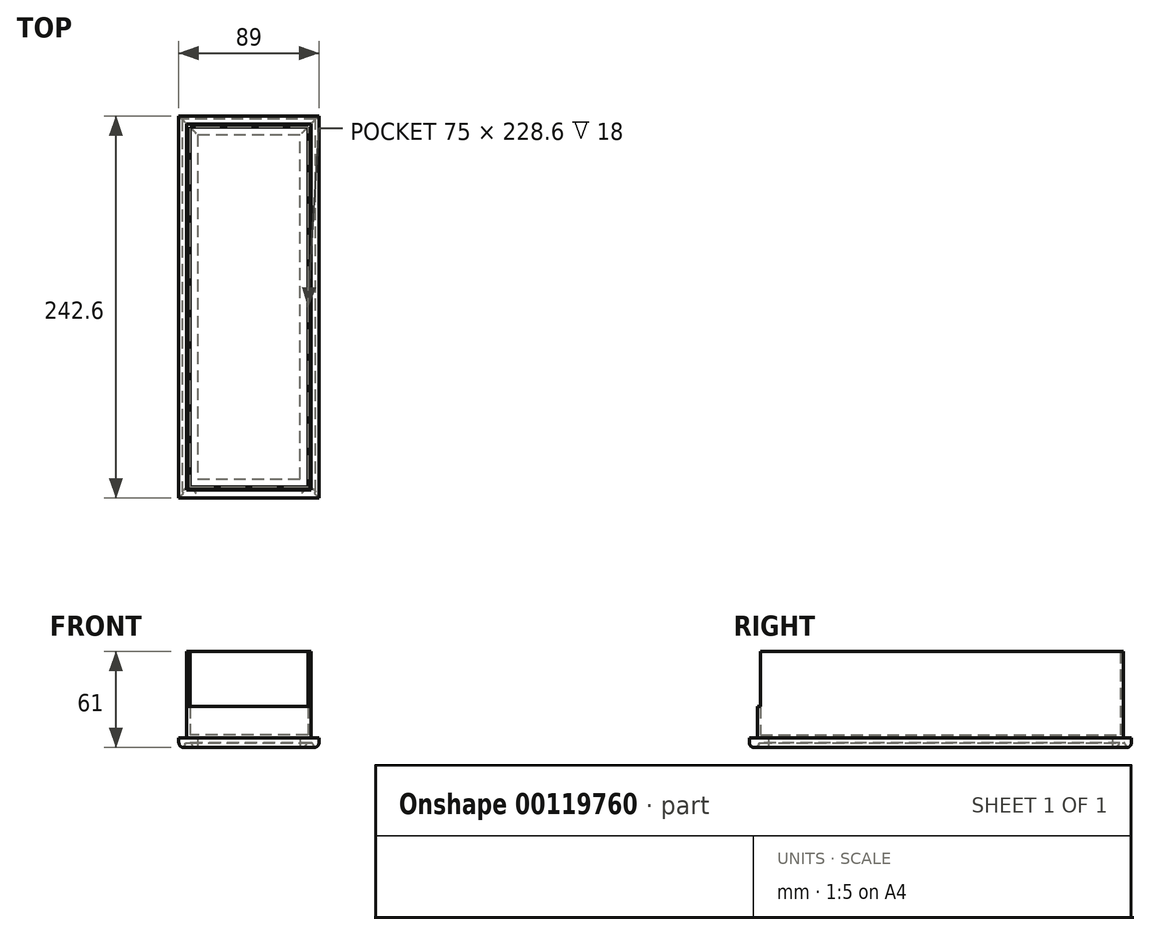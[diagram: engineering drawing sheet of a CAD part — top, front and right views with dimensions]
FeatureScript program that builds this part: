
annotation { "Feature Type Name" : "Feature", "Feature Type Description" : "" }
export const myFeature = defineFeature(function(context is Context, id is Id, definition is map)
    precondition{}
    {
        {
            var Q0;
            Q0=qCreatedBy(makeId("Top.planeOp"),FACE);
            var sketch = newSketch(context, id + "F0", { "sketchPlane" : qUnion([Q0])});
            skLineSegment(sketch, "E0.bottom", {"start": v(37.5, -114.3) * mm, "end": v(-37.5, -114.3) * mm});
            skLineSegment(sketch, "E0.top", {"start": v(37.5, 114.3) * mm, "end": v(-37.5, 114.3) * mm});
            skLineSegment(sketch, "E0.left", {"start": v(37.5, -114.3) * mm, "end": v(37.5, 114.3) * mm});
            skLineSegment(sketch, "E0.right", {"start": v(-37.5, -114.3) * mm, "end": v(-37.5, 114.3) * mm});
            skPoint(sketch, "E0.middle", {"position": v(0, 0) * mm});
            skSolve(sketch);
        }
        {
            var Q0;
            Q0 = qSketchRegion(id + "F0", true);
            extrude(context, id + "F1", {"entities" : qUnion([Q0]), "depth" : 2 * mm});
        }
        {
            var Q0;
            Q0=makeQuery(id+"F1.opExtrude","SWEPT_FACE",FACE,{"disambiguationData":[OSD([sQuery(id+"F0.wireOp",EDGE,"E0.right")])]});
            var sketch = newSketch(context, id + "F2", { "sketchPlane" : qUnion([Q0])});
            skLineSegment(sketch, "E1.bottom", {"start": v(-114.3, 0) * mm, "end": v(114.3, 0) * mm});
            skLineSegment(sketch, "E1.top", {"start": v(-114.3, 55) * mm, "end": v(114.3, 55) * mm});
            skLineSegment(sketch, "E1.left", {"start": v(-114.3, 0) * mm, "end": v(-114.3, 55) * mm});
            skLineSegment(sketch, "E1.right", {"start": v(114.3, 0) * mm, "end": v(114.3, 55) * mm});
            skSolve(sketch);
        }
        {
            var Q0;
            Q0 = qSketchRegion(id + "F2", true);
            extrude(context, id + "F3", {"entities" : qUnion([Q0]), "operationType" : NewBodyOperationType.ADD, "depth" : 2 * mm});
        }
        {
            var Q0;
            Q0=makeQuery(id+"F3.boolean.opBoolean","MERGE",FACE,{"derivedFrom":[makeQuery(id+"F1.opExtrude","SWEPT_FACE",FACE,{"disambiguationData":[OSD([sQuery(id+"F0.wireOp",EDGE,"E0.top")])]}),makeQuery(id+"F3.opExtrude","SWEPT_FACE",FACE,{"disambiguationData":[OSD([sQuery(id+"F2.wireOp",EDGE,"E1.left")])]})]});
            var sketch = newSketch(context, id + "F4", { "sketchPlane" : qUnion([Q0])});
            skLineSegment(sketch, "E2.bottom", {"start": v(39.5, 0) * mm, "end": v(-37.5, 0) * mm});
            skLineSegment(sketch, "E2.top", {"start": v(39.5, 55) * mm, "end": v(-37.5, 55) * mm});
            skLineSegment(sketch, "E2.left", {"start": v(39.5, 0) * mm, "end": v(39.5, 55) * mm});
            skLineSegment(sketch, "E2.right", {"start": v(-37.5, 0) * mm, "end": v(-37.5, 55) * mm});
            skSolve(sketch);
        }
        {
            var Q0;
            Q0 = qSketchRegion(id + "F4", true);
            extrude(context, id + "F5", {"entities" : qUnion([Q0]), "operationType" : NewBodyOperationType.ADD, "depth" : 2 * mm});
        }
        {
            var Q0;
            Q0=makeQuery(id+"F5.boolean.opBoolean","MERGE",FACE,{"derivedFrom":[makeQuery(id+"F1.opExtrude","SWEPT_FACE",FACE,{"disambiguationData":[OSD([sQuery(id+"F0.wireOp",EDGE,"E0.left")])]}),makeQuery(id+"F5.opExtrude","SWEPT_FACE",FACE,{"disambiguationData":[OSD([sQuery(id+"F4.wireOp",EDGE,"E2.right")])]})]});
            var sketch = newSketch(context, id + "F6", { "sketchPlane" : qUnion([Q0])});
            skLineSegment(sketch, "E3.bottom", {"start": v(116.3, 0) * mm, "end": v(-114.3, 0) * mm});
            skLineSegment(sketch, "E3.top", {"start": v(116.3, 55) * mm, "end": v(-114.3, 55) * mm});
            skLineSegment(sketch, "E3.left", {"start": v(116.3, 0) * mm, "end": v(116.3, 55) * mm});
            skLineSegment(sketch, "E3.right", {"start": v(-114.3, 0) * mm, "end": v(-114.3, 55) * mm});
            skSolve(sketch);
        }
        {
            var Q0;
            Q0 = qSketchRegion(id + "F6", true);
            extrude(context, id + "F7", {"entities" : qUnion([Q0]), "operationType" : NewBodyOperationType.ADD, "depth" : 2 * mm});
        }
        {
            var Q0;
            Q0=makeQuery(id+"F7.boolean.opBoolean","MERGE",FACE,{"derivedFrom":[makeQuery(id+"F3.boolean.opBoolean","MERGE",FACE,{"derivedFrom":[makeQuery(id+"F1.opExtrude","SWEPT_FACE",FACE,{"disambiguationData":[OSD([sQuery(id+"F0.wireOp",EDGE,"E0.bottom")])]}),makeQuery(id+"F3.opExtrude","SWEPT_FACE",FACE,{"disambiguationData":[OSD([sQuery(id+"F2.wireOp",EDGE,"E1.right")])]})]}),makeQuery(id+"F7.opExtrude","SWEPT_FACE",FACE,{"disambiguationData":[OSD([sQuery(id+"F6.wireOp",EDGE,"E3.right")])]})]});
            var sketch = newSketch(context, id + "F8", { "sketchPlane" : qUnion([Q0])});
            skLineSegment(sketch, "E4.bottom", {"start": v(-39.5, 0) * mm, "end": v(39.5, 0) * mm});
            skLineSegment(sketch, "E4.top", {"start": v(-39.5, 20) * mm, "end": v(39.5, 20) * mm});
            skLineSegment(sketch, "E4.left", {"start": v(-39.5, 0) * mm, "end": v(-39.5, 20) * mm});
            skLineSegment(sketch, "E4.right", {"start": v(39.5, 0) * mm, "end": v(39.5, 20) * mm});
            skSolve(sketch);
        }
        {
            var Q0;
            Q0 = qSketchRegion(id + "F8", true);
            extrude(context, id + "F9", {"entities" : qUnion([Q0]), "operationType" : NewBodyOperationType.ADD, "depth" : 2 * mm});
        }
        {
            var Q0;
            Q0=makeQuery(id+"F9.boolean.opBoolean","MERGE",FACE,{"derivedFrom":[makeQuery(id+"F7.boolean.opBoolean","MERGE",FACE,{"derivedFrom":[makeQuery(id+"F5.boolean.opBoolean","MERGE",FACE,{"derivedFrom":[makeQuery(id+"F3.boolean.opBoolean","MERGE",FACE,{"derivedFrom":[makeQuery(id+"F1.opExtrude","CAP_FACE",FACE,{"disambiguationData":[OSD([sQuery(id+"F0.wireOp",EDGE,"E0.bottom"),sQuery(id+"F0.wireOp",EDGE,"E0.top"),sQuery(id+"F0.wireOp",EDGE,"E0.left"),sQuery(id+"F0.wireOp",EDGE,"E0.right")])],"isStart":true}),makeQuery(id+"F3.opExtrude","SWEPT_FACE",FACE,{"disambiguationData":[OSD([sQuery(id+"F2.wireOp",EDGE,"E1.bottom")])]})]}),makeQuery(id+"F5.opExtrude","SWEPT_FACE",FACE,{"disambiguationData":[OSD([sQuery(id+"F4.wireOp",EDGE,"E2.bottom")])]})]}),makeQuery(id+"F7.opExtrude","SWEPT_FACE",FACE,{"disambiguationData":[OSD([sQuery(id+"F6.wireOp",EDGE,"E3.bottom")])]})]}),makeQuery(id+"F9.opExtrude","SWEPT_FACE",FACE,{"disambiguationData":[OSD([sQuery(id+"F8.wireOp",EDGE,"E4.bottom")])]})]});
            var sketch = newSketch(context, id + "F10", { "sketchPlane" : qUnion([Q0])});
            skLineSegment(sketch, "E5.0", {"start": v(44.5, -121.3) * mm, "end": v(44.5, 121.3) * mm});
            skLineSegment(sketch, "E5.1", {"start": v(-44.5, -121.3) * mm, "end": v(44.5, -121.3) * mm});
            skLineSegment(sketch, "E5.2", {"start": v(-44.5, 121.3) * mm, "end": v(-44.5, -121.3) * mm});
            skLineSegment(sketch, "E5.3", {"start": v(44.5, 121.3) * mm, "end": v(-44.5, 121.3) * mm});
            skSolve(sketch);
        }
        {
            var Q0;
            Q0 = qSketchRegion(id + "F10", true);
            extrude(context, id + "F11", {"entities" : qUnion([Q0]), "operationType" : NewBodyOperationType.ADD, "depth" : 6 * mm});
        }
        {
            var Q0;
            Q0=makeQuery(id+"F11.opExtrude","CAP_FACE",FACE,{"disambiguationData":[OSD([sQuery(id+"F10.wireOp",EDGE,"E5.0"),sQuery(id+"F10.wireOp",EDGE,"E5.1"),sQuery(id+"F10.wireOp",EDGE,"E5.2"),sQuery(id+"F10.wireOp",EDGE,"E5.3")])],"isStart":false});
            var sketch = newSketch(context, id + "F12", { "sketchPlane" : qUnion([Q0])});
            skLineSegment(sketch, "E6.0.0", {"start": v(-37.5, 114.3) * mm, "end": v(-37.5, -114.3) * mm});
            skLineSegment(sketch, "E6.0.1", {"start": v(-37.5, -114.3) * mm, "end": v(37.5, -114.3) * mm});
            skLineSegment(sketch, "E6.0.2", {"start": v(37.5, -114.3) * mm, "end": v(37.5, 114.3) * mm});
            skLineSegment(sketch, "E6.0.3", {"start": v(37.5, 114.3) * mm, "end": v(39.5, 114.3) * mm});
            skLineSegment(sketch, "E6.0.4", {"start": v(39.5, 114.3) * mm, "end": v(39.5, -116.3) * mm});
            skLineSegment(sketch, "E6.0.5", {"start": v(39.5, -116.3) * mm, "end": v(-39.5, -116.3) * mm});
            skLineSegment(sketch, "E6.0.6", {"start": v(-39.5, -116.3) * mm, "end": v(-39.5, 114.3) * mm});
            skLineSegment(sketch, "E6.0.7", {"start": v(-39.5, 114.3) * mm, "end": v(-37.5, 114.3) * mm});
            skLineSegment(sketch, "E7.0", {"start": v(-40.5, 115.3) * mm, "end": v(-36.5, 115.3) * mm});
            skLineSegment(sketch, "E7.1", {"start": v(-40.5, -117.3) * mm, "end": v(-40.5, 115.3) * mm});
            skLineSegment(sketch, "E7.2", {"start": v(-36.5, 115.3) * mm, "end": v(-36.5, -113.3) * mm});
            skLineSegment(sketch, "E7.3", {"start": v(40.5, -117.3) * mm, "end": v(-40.5, -117.3) * mm});
            skLineSegment(sketch, "E7.4", {"start": v(-36.5, -113.3) * mm, "end": v(36.5, -113.3) * mm});
            skLineSegment(sketch, "E7.5", {"start": v(36.5, -113.3) * mm, "end": v(36.5, 115.3) * mm});
            skLineSegment(sketch, "E7.6", {"start": v(36.5, 115.3) * mm, "end": v(40.5, 115.3) * mm});
            skLineSegment(sketch, "E7.7", {"start": v(40.5, 115.3) * mm, "end": v(40.5, -117.3) * mm});
            skLineSegment(sketch, "E8.0", {"start": v(-49.5, -126.3) * mm, "end": v(49.5, -126.3) * mm});
            skLineSegment(sketch, "E8.1", {"start": v(-49.5, 126.3) * mm, "end": v(-49.5, -126.3) * mm});
            skLineSegment(sketch, "E8.2", {"start": v(49.5, 126.3) * mm, "end": v(-49.5, 126.3) * mm});
            skLineSegment(sketch, "E8.3", {"start": v(49.5, -126.3) * mm, "end": v(49.5, 126.3) * mm});
            skSolve(sketch);
        }
        {
            var Q0;
            Q0=makeQuery(id+"F12.imprint","IMPRINT",FACE,{"disambiguationData":[TD([[makeQuery(id+"F12.imprint","IMPRINT",EDGE,{"derivedFrom":sQuery(id+"F12.wireOp",EDGE,"E6.0.0")}),1.0]])]});
            var Q1;
            Q1=makeQuery(id+"F12.imprint","IMPRINT",FACE,{"disambiguationData":[TD([[makeQuery(id+"F12.imprint","IMPRINT",EDGE,{"derivedFrom":sQuery(id+"F12.wireOp",EDGE,"E6.0.0")}),-1.0]])]});
            extrude(context, id + "F13", {"entities" : qUnion([Q0, Q1]), "operationType" : NewBodyOperationType.REMOVE, "oppositeDirection" : true, "depth" : 3 * mm});
        }
        {
            var Q0;
            Q0=makeQuery(id+"F13.boolean.opBoolean","COPY",FACE,{"derivedFrom":makeQuery(id+"F13.opExtrude","CAP_FACE",FACE,{"disambiguationData":[OSD([sQuery(id+"F12.wireOp",EDGE,"E7.0"),sQuery(id+"F12.wireOp",EDGE,"E7.1"),sQuery(id+"F12.wireOp",EDGE,"E7.2"),sQuery(id+"F12.wireOp",EDGE,"E7.3"),sQuery(id+"F12.wireOp",EDGE,"E7.4"),sQuery(id+"F12.wireOp",EDGE,"E7.5"),sQuery(id+"F12.wireOp",EDGE,"E7.6"),sQuery(id+"F12.wireOp",EDGE,"E7.7")])],"isStart":false})});
            fillet(context, id + "F14", {"entities" : qUnion([Q0]), "radius" : .8 * mm, "tangentPropagation" : true, "allowEdgeOverflow" : false});
        }
        {
            var Q0;
            Q0=makeQuery(id+"F11.opExtrude","CAP_FACE",FACE,{"disambiguationData":[OSD([sQuery(id+"F10.wireOp",EDGE,"E5.0"),sQuery(id+"F10.wireOp",EDGE,"E5.1"),sQuery(id+"F10.wireOp",EDGE,"E5.2"),sQuery(id+"F10.wireOp",EDGE,"E5.3")])],"isStart":false});
            fillet(context, id + "F15", {"entities" : qUnion([Q0]), "radius" : 3 * mm, "tangentPropagation" : true, "allowEdgeOverflow" : false});
        }
        {
            var Q0;
            Q0=makeQuery(id+"F11.opExtrude","CAP_FACE",FACE,{"disambiguationData":[OSD([sQuery(id+"F10.wireOp",EDGE,"E5.0"),sQuery(id+"F10.wireOp",EDGE,"E5.1"),sQuery(id+"F10.wireOp",EDGE,"E5.2"),sQuery(id+"F10.wireOp",EDGE,"E5.3")])],"isStart":false});
            var sketch = newSketch(context, id + "F16", { "sketchPlane" : qUnion([Q0])});
            skLineSegment(sketch, "E9.0.0", {"start": v(-37.5, 114.3) * mm, "end": v(37.5, 114.3) * mm});
            skLineSegment(sketch, "E9.0.1", {"start": v(37.5, 114.3) * mm, "end": v(37.5, -114.3) * mm});
            skLineSegment(sketch, "E9.0.2", {"start": v(37.5, -114.3) * mm, "end": v(-37.5, -114.3) * mm});
            skLineSegment(sketch, "E9.0.3", {"start": v(-37.5, -114.3) * mm, "end": v(-37.5, 114.3) * mm});
            skLineSegment(sketch, "E10.0", {"start": v(-32.5, -109.3) * mm, "end": v(-32.5, 109.3) * mm});
            skLineSegment(sketch, "E10.1", {"start": v(32.5, -109.3) * mm, "end": v(-32.5, -109.3) * mm});
            skLineSegment(sketch, "E10.2", {"start": v(32.5, 109.3) * mm, "end": v(32.5, -109.3) * mm});
            skLineSegment(sketch, "E10.3", {"start": v(-32.5, 109.3) * mm, "end": v(32.5, 109.3) * mm});
            skSolve(sketch);
        }
        {
            var Q0;
            Q0=makeQuery(id+"F16.imprint","IMPRINT",FACE,{"disambiguationData":[TD([[makeQuery(id+"F16.imprint","IMPRINT",EDGE,{"derivedFrom":sQuery(id+"F16.wireOp",EDGE,"E10.0")}),-1.0]])]});
            extrude(context, id + "F17", {"entities" : qUnion([Q0]), "operationType" : NewBodyOperationType.REMOVE, "oppositeDirection" : true, "depth" : 6 * mm});
        }
    });
